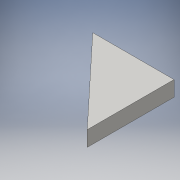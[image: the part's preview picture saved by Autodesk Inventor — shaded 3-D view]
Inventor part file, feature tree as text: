
AUTODESK INVENTOR PART (.ipt)
format: ipt  version: 2016 (Build 200138000, 138)  size: 83,968 bytes
history: native  units: mm
features: other x1, extrude x1, sketch x1
ambient origin geometry x8: Origin, YZ Plane, XZ Plane, XY Plane, X Axis, Y Axis, Z Axis, Center Point
bodies: Body1 (feature_tree)
feature tree (3):
  other  "Sólido1"
  extrude  "Extrusión1"  [1 undecoded]
  sketch  "Boceto1"  dims[d0=3.0mm d1=0.0mm]
note: 1 required parameter value undecoded (feature->parameter linkage not recoverable at this tier; creation-order binding heuristic only, values carry confidence <= 0.55)
